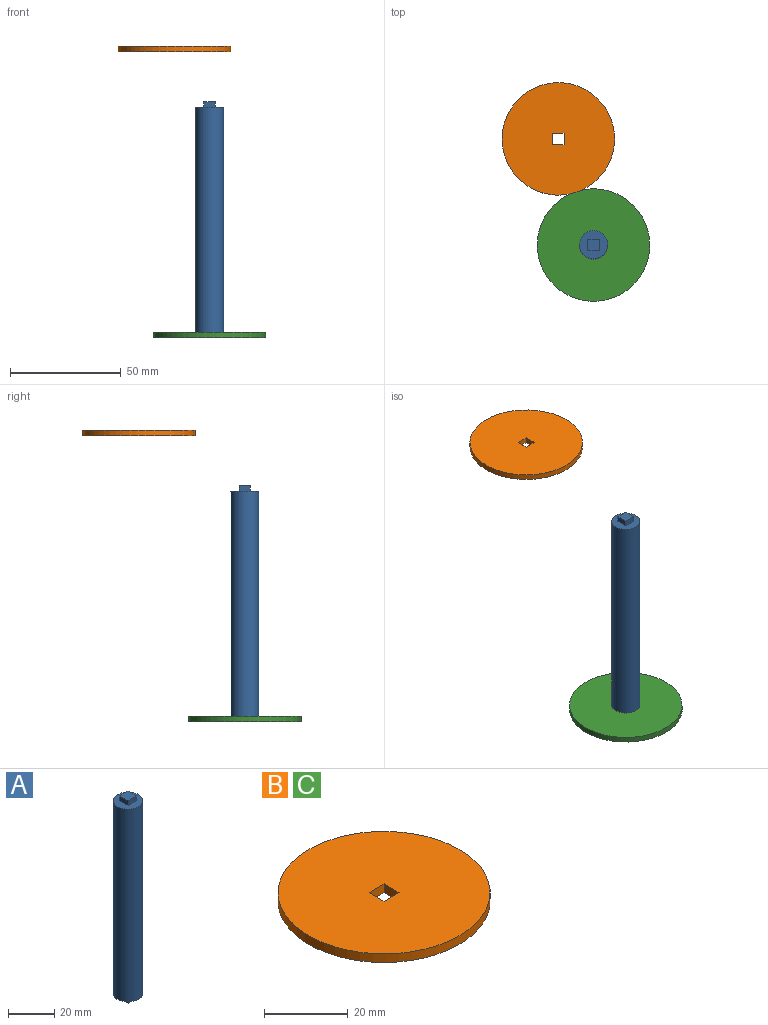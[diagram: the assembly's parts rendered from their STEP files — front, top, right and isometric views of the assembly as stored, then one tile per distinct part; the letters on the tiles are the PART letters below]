
ASSEMBLY  parts=3 mates=1
PART A: 13 faces, bbox 12.7x12.7x106.7 mm
  f0: plane 12.7x12.7mm, normal (0,0,1), area 100.9mm2, adj f1,f3,f4,f5,f6
  f1: cylinder r=6.35mm len=101.6mm, axis (0,0,-1), area 4053.7mm2, adj f0,f2
  f2: plane 12.7x12.7mm, normal (0,0,-1), area 100.9mm2, adj f1,f8,f9,f10,f11
  f3: plane 5.08x2.54mm, normal (0,-1,0), area 12.9mm2, adj f0,f4,f6,f7
  f4: plane 5.08x2.54mm, normal (1,0,0), area 12.9mm2, adj f0,f3,f5,f7
  f5: plane 5.08x2.54mm, normal (0,1,0), area 12.9mm2, adj f0,f4,f6,f7
  f6: plane 5.08x2.54mm, normal (-1,0,0), area 12.9mm2, adj f0,f3,f5,f7
  f7: plane 5.08x5.08mm, normal (0,0,1), area 25.8mm2, adj f3,f4,f5,f6
  f8: plane 5.08x2.54mm, normal (0,1,0), area 12.9mm2, adj f2,f9,f11,f12
  f9: plane 5.08x2.54mm, normal (1,0,0), area 12.9mm2, adj f2,f8,f10,f12
  f10: plane 5.08x2.54mm, normal (0,-1,0), area 12.9mm2, adj f2,f9,f11,f12
  f11: plane 5.08x2.54mm, normal (-1,0,0), area 12.9mm2, adj f2,f8,f10,f12
  f12: plane 5.08x5.08mm, normal (0,0,-1), area 25.8mm2, adj f8,f9,f10,f11
PART B: 7 faces, bbox 50.8x50.8x2.5 mm
  f0: plane 5.08x2.54mm, normal (0,-1,0), area 12.9mm2, adj f1,f4,f5,f6
  f1: plane 5.08x2.54mm, normal (-1,0,0), area 12.9mm2, adj f0,f2,f5,f6
  f2: plane 5.08x2.54mm, normal (0,1,0), area 12.9mm2, adj f1,f4,f5,f6
  f3: cylinder r=25.4mm len=50.8mm, axis (0,0,-1), area 405.4mm2, adj f5,f6
  f4: plane 5.08x2.54mm, normal (1,0,0), area 12.9mm2, adj f0,f2,f5,f6
  f5: plane 50.8x50.8mm, normal (0,0,1), area 2001mm2, adj f0,f1,f2,f3,f4
  f6: plane 50.8x50.8mm, normal (0,0,-1), area 2001mm2, adj f0,f1,f2,f3,f4
PART C: same geometry as B
PLACE A rot(axis=(0.71,-0.71,0),180deg) t=(30.08,87.51,24.72)mm
PLACE B t=(106.21,94.87,49.85)mm
PLACE C rot(axis=(0,0,-1),90deg) t=(38.93,-176.28,-79.42)mm
MATE fastened A.f3 <-> C.f0  axis (1,0,0) through (-28.67,-22.99,-78.15)mm
